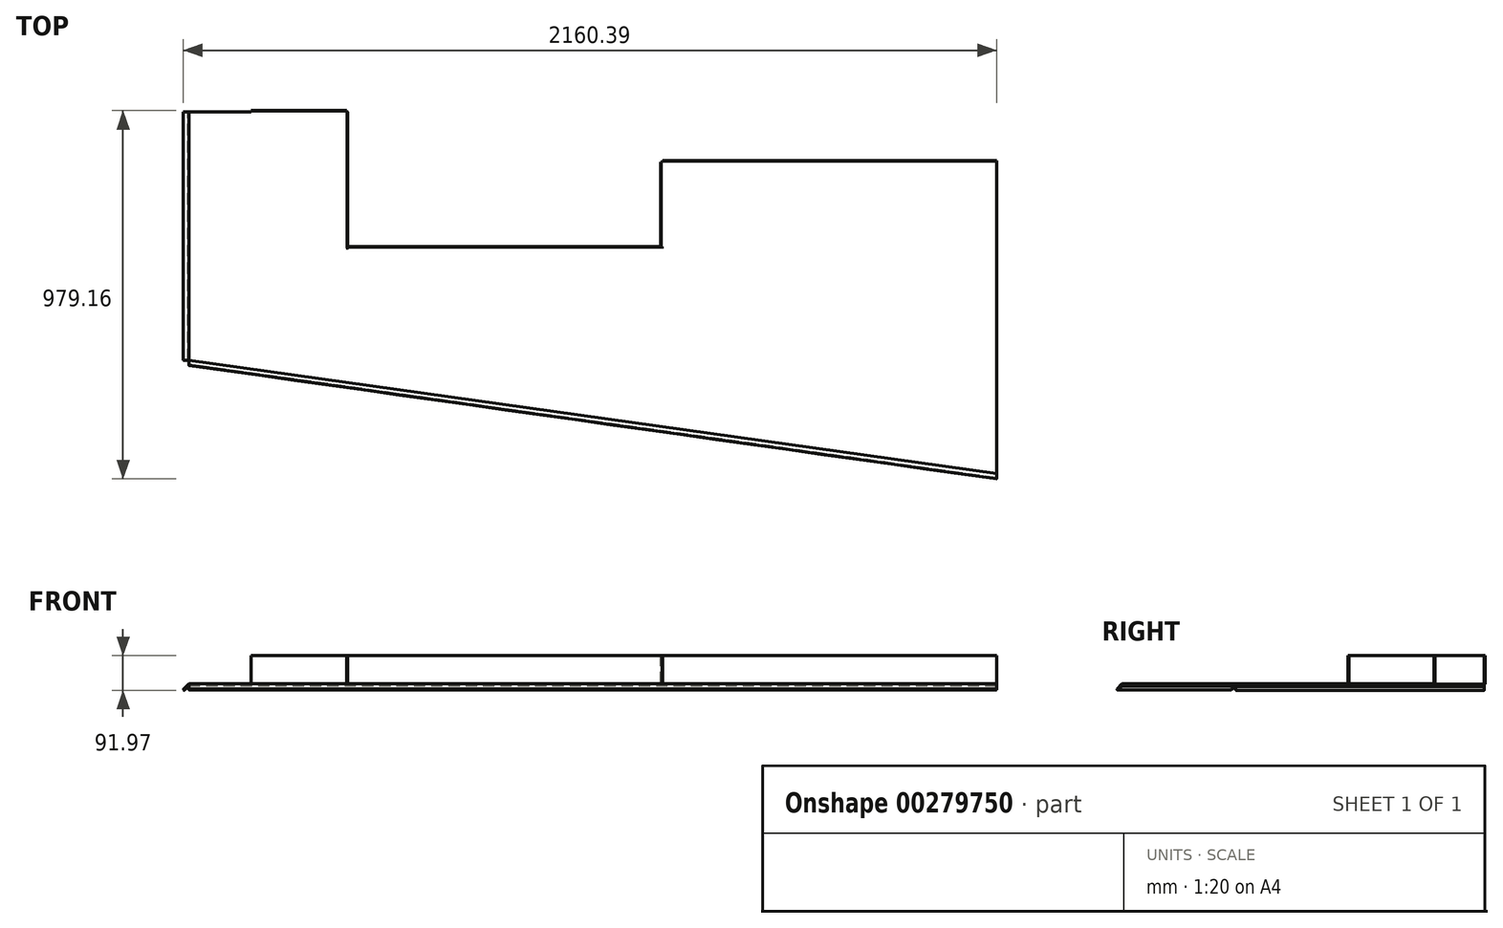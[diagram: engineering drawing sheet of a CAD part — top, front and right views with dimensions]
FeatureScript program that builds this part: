
annotation { "Feature Type Name" : "Feature", "Feature Type Description" : "" }
export const myFeature = defineFeature(function(context is Context, id is Id, definition is map)
    precondition{}
    {
        {
            var Q0;
            Q0=qCreatedBy(makeId("Top.planeOp"),FACE);
            var sketch = newSketch(context, id + "F0", { "sketchPlane" : qUnion([Q0])});
            skLineSegment(sketch, "E0", {"start": v(-902.65, 576.82) * mm, "end": v(-1321.75, 576.82) * mm});
            skLineSegment(sketch, "E1", {"start": v(-1321.75, 576.82) * mm, "end": v(-1321.75, -83.58) * mm});
            skLineSegment(sketch, "E2", {"start": v(-1321.75, -83.58) * mm, "end": v(824.55, -385.22) * mm});
            skLineSegment(sketch, "E3", {"start": v(824.55, -385.22) * mm, "end": v(824.55, 443.45) * mm});
            skLineSegment(sketch, "E4", {"start": v(824.55, 443.45) * mm, "end": v(-64.45, 443.45) * mm});
            skLineSegment(sketch, "E5", {"start": v(-64.45, 443.45) * mm, "end": v(-64.45, 214.85) * mm});
            skLineSegment(sketch, "E6", {"start": v(-64.45, 214.85) * mm, "end": v(-902.65, 214.85) * mm});
            skLineSegment(sketch, "E7", {"start": v(-902.65, 214.85) * mm, "end": v(-902.65, 576.82) * mm});
            skSolve(sketch);
        }
        {
            var Q0;
            Q0=makeQuery(id+"F0.imprint","IMPRINT",FACE,{"disambiguationData":[TD([[makeQuery(id+"F0.imprint","IMPRINT",EDGE,{"derivedFrom":sQuery(id+"F0.wireOp",EDGE,"E0")}),1.0]])]});
            extrude(context, id + "F1", {"entities" : qUnion([Q0]), "depth" : 1.31 * mm});
        }
        {
            var Q0;
            Q0=makeQuery(id+"F1.opExtrude","SWEPT_FACE",FACE,{"disambiguationData":[OSD([sQuery(id+"F0.wireOp",EDGE,"E3")])]});
            var sketch = newSketch(context, id + "F2", { "sketchPlane" : qUnion([Q0])});
            skLineSegment(sketch, "E8", {"start": v(-385.22, 1.31) * mm, "end": v(-398.7, -12.16) * mm});
            skArc(sketch, "E9", {"start": v(-398.7, -12.16) * mm, "mid": v(-398.7, -14.4) * mm, "end": v(-396.45, -14.4) * mm});
            skLineSegment(sketch, "E10", {"start": v(-385.22, 0) * mm, "end": v(-398.04, -12.82) * mm});
            skArc(sketch, "E11", {"start": v(-398.04, -12.82) * mm, "mid": v(-398.03, -13.75) * mm, "end": v(-397.1, -13.75) * mm});
            skLineSegment(sketch, "E12", {"start": v(-397.1, -13.75) * mm, "end": v(-387.1, -4.57) * mm});
            skLineSegment(sketch, "E13", {"start": v(-387.1, -4.57) * mm, "end": v(-386.47, -5.25) * mm});
            skLineSegment(sketch, "E14", {"start": v(-386.47, -5.25) * mm, "end": v(-396.45, -14.4) * mm});
            skSolve(sketch);
        }
        {
            var Q0;
            Q0=makeQuery(id+"F2.imprint","IMPRINT",FACE,{"disambiguationData":[TD([[makeQuery(id+"F2.imprint","IMPRINT",EDGE,{"derivedFrom":sQuery(id+"F2.wireOp",EDGE,"E8")}),1.0]])]});
            var Q1;
            Q1=makeQuery(id+"F1.opExtrude","CAP_EDGE",EDGE,{"disambiguationData":[OSD([sQuery(id+"F0.wireOp",EDGE,"E2")])],"isStart":false});
            sweep(context, id + "F3", {"operationType" : NewBodyOperationType.ADD, "profiles" : qUnion([Q0]), "path" : qUnion([Q1]), "keepProfileOrientation" : true});
        }
        {
            var Q0;
            Q0=makeQuery(id+"F1.opExtrude","SWEPT_FACE",FACE,{"disambiguationData":[OSD([sQuery(id+"F0.wireOp",EDGE,"E0")])]});
            var sketch = newSketch(context, id + "F4", { "sketchPlane" : qUnion([Q0])});
            skLineSegment(sketch, "E15", {"start": v(1321.75, 1.31) * mm, "end": v(1335.22, -12.16) * mm});
            skLineSegment(sketch, "E16", {"start": v(1321.75, 0) * mm, "end": v(1334.56, -12.82) * mm});
            skArc(sketch, "E17", {"start": v(1332.23, -15.15) * mm, "mid": v(1335.22, -15.15) * mm, "end": v(1335.22, -12.16) * mm});
            skLineSegment(sketch, "E18", {"start": v(1332.23, -15.15) * mm, "end": v(1323.25, -6.17) * mm});
            skLineSegment(sketch, "E19", {"start": v(1323.25, -6.17) * mm, "end": v(1323.68, -5.74) * mm});
            skLineSegment(sketch, "E20", {"start": v(1323.68, -5.74) * mm, "end": v(1332.9, -14.51) * mm});
            skArc(sketch, "E21", {"start": v(1332.9, -14.51) * mm, "mid": v(1334.57, -14.48) * mm, "end": v(1334.56, -12.82) * mm});
            skSolve(sketch);
        }
        {
            var Q0;
            Q0=makeQuery(id+"F4.imprint","IMPRINT",FACE,{"disambiguationData":[TD([[makeQuery(id+"F4.imprint","IMPRINT",EDGE,{"derivedFrom":sQuery(id+"F4.wireOp",EDGE,"E15")}),-1.0]])]});
            var Q1;
            {var subQ0=sQuery(id+"F0.wireOp",EDGE,"E2");Q1=makeQuery(id+"F3.boolean.opBoolean","MERGE",VERTEX,{"derivedFrom":[makeQuery(id+"F1.opExtrude","CAP_VERTEX",VERTEX,{"disambiguationData":[OSD([sQuery(id+"F0.wireOp",EDGE,"E1"),subQ0])],"isStart":false}),makeQuery(id+"F3.opSweep","CAP_VERTEX",VERTEX,{"disambiguationData":[OSD([subQ0,sQuery(id+"F0.wireOp",EDGE,"E3"),sQuery(id+"F2.wireOp",EDGE,"E8")])],"isStart":false})]});}
            extrude(context, id + "F5", {"entities" : qUnion([Q0]), "operationType" : NewBodyOperationType.ADD, "endBound" : BoundingType.UP_TO_VERTEX, "oppositeDirection" : true, "endBoundEntityVertex" : qUnion([Q1]), "depth" : 25.4 * mm});
        }
        {
            var Q0;
            Q0=makeQuery(id+"F1.opExtrude","SWEPT_FACE",FACE,{"disambiguationData":[OSD([sQuery(id+"F0.wireOp",EDGE,"E7")])]});
            var sketch = newSketch(context, id + "F6", { "sketchPlane" : qUnion([Q0])});
            skLineSegment(sketch, "E22", {"start": v(576.82, 0) * mm, "end": v(576.82, 0) * mm});
            skLineSegment(sketch, "E23", {"start": v(580, 3.18) * mm, "end": v(580, 76.2) * mm});
            skLineSegment(sketch, "E24", {"start": v(580, 76.2) * mm, "end": v(578.69, 76.2) * mm});
            skLineSegment(sketch, "E25", {"start": v(578.69, 76.2) * mm, "end": v(578.69, 4.49) * mm});
            skLineSegment(sketch, "E26", {"start": v(576.82, 1.31) * mm, "end": v(575.51, 1.31) * mm});
            skPoint(sketch, "E27.visualSharp", {"position": v(580, 0) * mm});
            skArc(sketch, "E27.filletArc", {"start": v(576.82, 0) * mm, "mid": v(579.07, 0.93) * mm, "end": v(580, 3.18) * mm});
            skPoint(sketch, "E28.visualSharp", {"position": v(578.69, 1.31) * mm});
            skArc(sketch, "E28.filletArc", {"start": v(575.51, 1.31) * mm, "mid": v(577.76, 2.24) * mm, "end": v(578.69, 4.49) * mm});
            skSolve(sketch);
        }
        {
            var Q0;
            {var subQ0=sQuery(id+"F0.wireOp",EDGE,"E0");Q0=makeQuery(id+"F5.boolean.opBoolean","MERGE",FACE,{"derivedFrom":[makeQuery(id+"F1.opExtrude","SWEPT_FACE",FACE,{"disambiguationData":[OSD([subQ0])]}),makeQuery(id+"F5.opExtrude","CAP_FACE",FACE,{"disambiguationData":[OSD([subQ0,sQuery(id+"F0.wireOp",EDGE,"E1"),sQuery(id+"F4.wireOp",EDGE,"E15"),sQuery(id+"F4.wireOp",EDGE,"E16"),sQuery(id+"F4.wireOp",EDGE,"E17"),sQuery(id+"F4.wireOp",EDGE,"E18"),sQuery(id+"F4.wireOp",EDGE,"E19"),sQuery(id+"F4.wireOp",EDGE,"E20"),sQuery(id+"F4.wireOp",EDGE,"E21")])],"isStart":true})]});}
            var sketch = newSketch(context, id + "F7", { "sketchPlane" : qUnion([Q0])});
            skLineSegment(sketch, "E29", {"start": v(902.65, 0) * mm, "end": v(902.65, 0) * mm});
            skLineSegment(sketch, "E30", {"start": v(899.47, 3.18) * mm, "end": v(899.47, 76.2) * mm});
            skLineSegment(sketch, "E31", {"start": v(899.47, 76.2) * mm, "end": v(900.78, 76.2) * mm});
            skLineSegment(sketch, "E32", {"start": v(900.78, 76.2) * mm, "end": v(900.78, 4.49) * mm});
            skPoint(sketch, "E33.visualSharp", {"position": v(899.47, 0) * mm});
            skArc(sketch, "E33.filletArc", {"start": v(899.47, 3.17) * mm, "mid": v(900.4, 0.93) * mm, "end": v(902.65, 0) * mm});
            skPoint(sketch, "E34.visualSharp", {"position": v(900.78, 1.31) * mm});
            skArc(sketch, "E34.filletArc", {"start": v(900.78, 4.49) * mm, "mid": v(901.71, 2.24) * mm, "end": v(903.96, 1.31) * mm});
            skSolve(sketch);
        }
        {
            var Q0;
            Q0=makeQuery(id+"F6.imprint","IMPRINT",FACE,{"disambiguationData":[TD([[makeQuery(id+"F6.imprint","IMPRINT",EDGE,{"derivedFrom":sQuery(id+"F6.wireOp",EDGE,"E23")}),1.0]])]});
            extrude(context, id + "F8", {"entities" : qUnion([Q0]), "operationType" : NewBodyOperationType.ADD, "oppositeDirection" : true, "depth" : 254 * mm});
        }
        {
            var Q0;
            Q0=makeQuery(id+"F7.imprint","IMPRINT",FACE,{"disambiguationData":[TD([[makeQuery(id+"F7.imprint","IMPRINT",EDGE,{"derivedFrom":sQuery(id+"F7.wireOp",EDGE,"E30")}),-1.0]])]});
            var Q1;
            Q1=makeQuery(id+"F1.opExtrude","SWEPT_FACE",FACE,{"disambiguationData":[OSD([sQuery(id+"F0.wireOp",EDGE,"E6")])]});
            extrude(context, id + "F9", {"entities" : qUnion([Q0]), "operationType" : NewBodyOperationType.ADD, "endBound" : BoundingType.UP_TO_SURFACE, "oppositeDirection" : true, "endBoundEntityFace" : qUnion([Q1]), "depth" : 25.4 * mm});
        }
        {
            var Q0;
            Q0=makeQuery(id+"F1.opExtrude","SWEPT_FACE",FACE,{"disambiguationData":[OSD([sQuery(id+"F0.wireOp",EDGE,"E5")])]});
            var sketch = newSketch(context, id + "F10", { "sketchPlane" : qUnion([Q0])});
            skLineSegment(sketch, "E35", {"start": v(-216.72, 4.49) * mm, "end": v(-216.72, 76.2) * mm});
            skLineSegment(sketch, "E36", {"start": v(-216.72, 76.2) * mm, "end": v(-218.03, 76.2) * mm});
            skLineSegment(sketch, "E37", {"start": v(-218.03, 76.2) * mm, "end": v(-218.03, 3.18) * mm});
            skLineSegment(sketch, "E38", {"start": v(-214.85, 0) * mm, "end": v(-214.85, 0) * mm});
            skPoint(sketch, "E39.visualSharp", {"position": v(-218.03, 0) * mm});
            skArc(sketch, "E39.filletArc", {"start": v(-218.03, 3.17) * mm, "mid": v(-217.1, 0.93) * mm, "end": v(-214.85, 0) * mm});
            skPoint(sketch, "E40.visualSharp", {"position": v(-216.72, 1.31) * mm});
            skArc(sketch, "E40.filletArc", {"start": v(-216.72, 4.49) * mm, "mid": v(-215.79, 2.24) * mm, "end": v(-213.54, 1.31) * mm});
            skLineSegment(sketch, "E41", {"start": v(-214.85, 0) * mm, "end": v(-214.85, 1.31) * mm});
            skLineSegment(sketch, "E42", {"start": v(-214.85, 1.31) * mm, "end": v(-213.54, 1.31) * mm});
            skSolve(sketch);
        }
        {
            var Q0;
            Q0 = qSketchRegion(id + "F10", true);
            var Q1;
            Q1=makeQuery(id+"F9.opExtrude","SWEPT_FACE",FACE,{"disambiguationData":[OSD([sQuery(id+"F7.wireOp",EDGE,"E30")])]});
            extrude(context, id + "F11", {"entities" : qUnion([Q0]), "operationType" : NewBodyOperationType.ADD, "endBound" : BoundingType.UP_TO_SURFACE, "endBoundEntityFace" : qUnion([Q1]), "depth" : 25.4 * mm});
        }
        {
            var Q0;
            Q0=makeQuery(id+"F1.opExtrude","SWEPT_FACE",FACE,{"disambiguationData":[OSD([sQuery(id+"F0.wireOp",EDGE,"E4")])]});
            var sketch = newSketch(context, id + "F12", { "sketchPlane" : qUnion([Q0])});
            skLineSegment(sketch, "E43", {"start": v(64.45, 0) * mm, "end": v(64.45, 0) * mm});
            skLineSegment(sketch, "E44", {"start": v(67.62, 3.17) * mm, "end": v(67.62, 76.2) * mm});
            skLineSegment(sketch, "E45", {"start": v(67.62, 76.2) * mm, "end": v(66.31, 76.2) * mm});
            skLineSegment(sketch, "E46", {"start": v(66.31, 76.2) * mm, "end": v(66.31, 4.49) * mm});
            skLineSegment(sketch, "E47", {"start": v(64.45, 1.31) * mm, "end": v(63.14, 1.31) * mm});
            skPoint(sketch, "E48.visualSharp", {"position": v(67.62, 0) * mm});
            skArc(sketch, "E48.filletArc", {"start": v(64.45, 0) * mm, "mid": v(66.7, 0.93) * mm, "end": v(67.62, 3.17) * mm});
            skPoint(sketch, "E49.visualSharp", {"position": v(66.31, 1.31) * mm});
            skArc(sketch, "E49.filletArc", {"start": v(63.14, 1.31) * mm, "mid": v(65.38, 2.24) * mm, "end": v(66.31, 4.49) * mm});
            skLineSegment(sketch, "E50", {"start": v(64.45, 1.31) * mm, "end": v(64.45, 0) * mm});
            skSolve(sketch);
        }
        {
            var Q0;
            Q0 = qSketchRegion(id + "F12", true);
            var Q1;
            Q1=makeQuery(id+"F11.opExtrude","SWEPT_FACE",FACE,{"disambiguationData":[OSD([sQuery(id+"F10.wireOp",EDGE,"E37")])]});
            extrude(context, id + "F13", {"entities" : qUnion([Q0]), "operationType" : NewBodyOperationType.ADD, "endBound" : BoundingType.UP_TO_SURFACE, "oppositeDirection" : true, "endBoundEntityFace" : qUnion([Q1]), "depth" : 25.4 * mm});
        }
        {
            var Q0;
            {var subQ0=sQuery(id+"F0.wireOp",EDGE,"E3");Q0=makeQuery(id+"F3.boolean.opBoolean","MERGE",FACE,{"derivedFrom":[makeQuery(id+"F1.opExtrude","SWEPT_FACE",FACE,{"disambiguationData":[OSD([subQ0])]}),makeQuery(id+"F3.opSweep","CAP_FACE",FACE,{"disambiguationData":[OSD([sQuery(id+"F0.wireOp",EDGE,"E2"),subQ0,sQuery(id+"F2.wireOp",EDGE,"E8"),sQuery(id+"F2.wireOp",EDGE,"E9"),sQuery(id+"F2.wireOp",EDGE,"E10"),sQuery(id+"F2.wireOp",EDGE,"E11"),sQuery(id+"F2.wireOp",EDGE,"E12"),sQuery(id+"F2.wireOp",EDGE,"E13"),sQuery(id+"F2.wireOp",EDGE,"E14")])],"isStart":true})]});}
            var sketch = newSketch(context, id + "F14", { "sketchPlane" : qUnion([Q0])});
            skLineSegment(sketch, "E51", {"start": v(443.45, 0) * mm, "end": v(443.45, 0) * mm});
            skLineSegment(sketch, "E52", {"start": v(446.63, 3.18) * mm, "end": v(446.63, 76.2) * mm});
            skLineSegment(sketch, "E53", {"start": v(446.63, 76.2) * mm, "end": v(445.32, 76.2) * mm});
            skLineSegment(sketch, "E54", {"start": v(445.32, 76.2) * mm, "end": v(445.32, 4.49) * mm});
            skLineSegment(sketch, "E55", {"start": v(443.45, 1.31) * mm, "end": v(442.14, 1.31) * mm});
            skLineSegment(sketch, "E56", {"start": v(443.45, 1.31) * mm, "end": v(443.45, 0) * mm});
            skPoint(sketch, "E57.visualSharp", {"position": v(446.63, 0) * mm});
            skArc(sketch, "E57.filletArc", {"start": v(443.45, 0) * mm, "mid": v(445.7, 0.93) * mm, "end": v(446.63, 3.18) * mm});
            skPoint(sketch, "E58.visualSharp", {"position": v(445.32, 1.31) * mm});
            skArc(sketch, "E58.filletArc", {"start": v(442.14, 1.31) * mm, "mid": v(444.39, 2.24) * mm, "end": v(445.32, 4.49) * mm});
            skSolve(sketch);
        }
        {
            var Q0;
            Q0 = qSketchRegion(id + "F14", true);
            var Q1;
            Q1=makeQuery(id+"F13.opExtrude","CAP_VERTEX",VERTEX,{"disambiguationData":[OSD([sQuery(id+"F0.wireOp",EDGE,"E4"),sQuery(id+"F12.wireOp",EDGE,"E47"),sQuery(id+"F12.wireOp",EDGE,"E49.filletArc")])],"isStart":true});
            extrude(context, id + "F15", {"entities" : qUnion([Q0]), "operationType" : NewBodyOperationType.ADD, "endBound" : BoundingType.UP_TO_VERTEX, "oppositeDirection" : true, "endBoundEntityVertex" : qUnion([Q1]), "depth" : 25.4 * mm});
        }
    });
